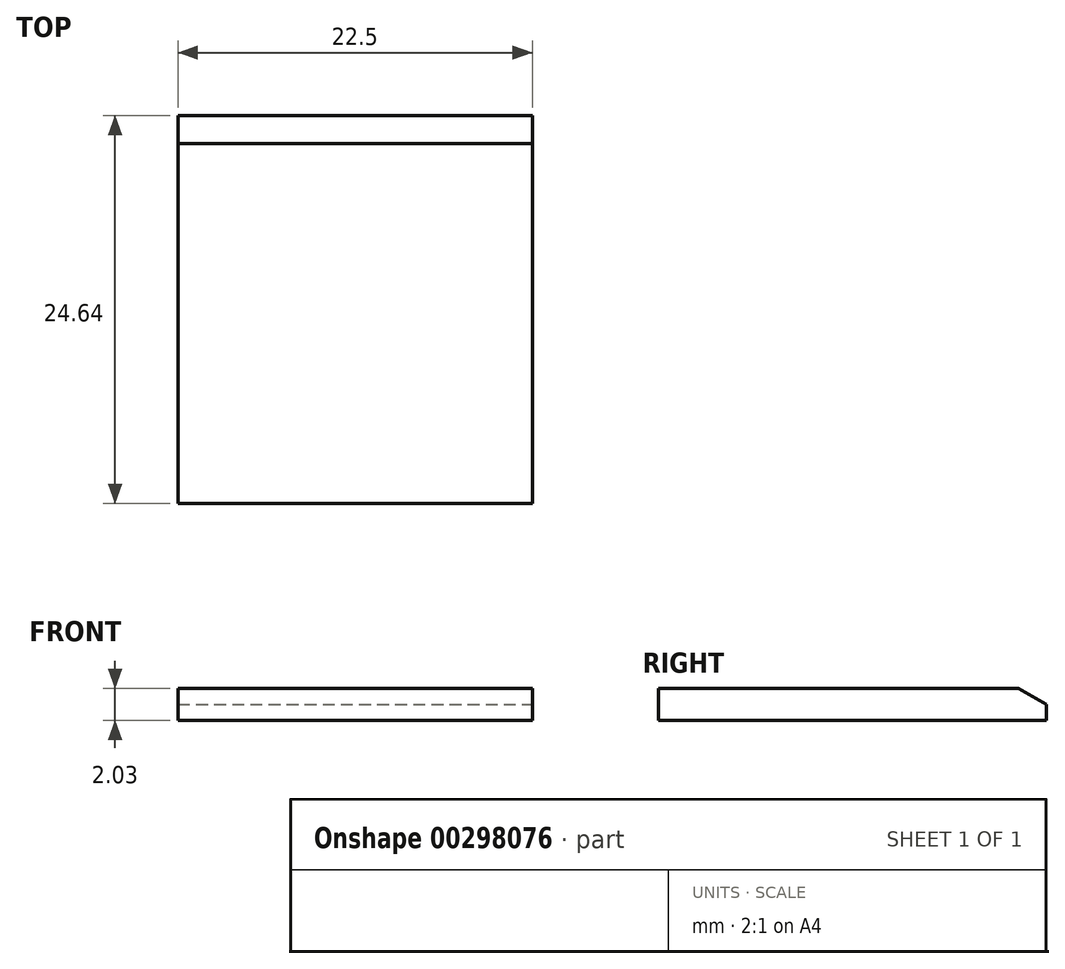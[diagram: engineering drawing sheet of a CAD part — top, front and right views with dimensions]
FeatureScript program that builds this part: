
annotation { "Feature Type Name" : "Feature", "Feature Type Description" : "" }
export const myFeature = defineFeature(function(context is Context, id is Id, definition is map)
    precondition{}
    {
        {
            var Q0;
            Q0=qCreatedBy(makeId("Front.planeOp"),FACE);
            var sketch = newSketch(context, id + "F0", { "sketchPlane" : qUnion([Q0])});
            skLineSegment(sketch, "E0.bottom", {"start": v(11.43, 1.27) * mm, "end": v(-11.43, 1.27) * mm});
            skLineSegment(sketch, "E0.top", {"start": v(11.43, -1.27) * mm, "end": v(-11.43, -1.27) * mm});
            skLineSegment(sketch, "E0.left", {"start": v(11.43, 1.27) * mm, "end": v(11.43, -1.27) * mm});
            skLineSegment(sketch, "E0.right", {"start": v(-11.43, 1.27) * mm, "end": v(-11.43, -1.27) * mm});
            skPoint(sketch, "E0.middle", {"position": v(0, 0) * mm});
            skSolve(sketch);
        }
        {
            var Q0;
            Q0=makeQuery(id+"F0.imprint","IMPRINT",FACE,{"disambiguationData":[TD([[makeQuery(id+"F0.imprint","IMPRINT",EDGE,{"derivedFrom":sQuery(id+"F0.wireOp",EDGE,"E0.bottom")}),1.0]])]});
            extrude(context, id + "F1", {"entities" : qUnion([Q0]), "depth" : 24.64 * mm});
        }
        {
            var Q0;
            Q0=makeQuery(id+"F1.opExtrude","CAP_EDGE",EDGE,{"disambiguationData":[OSD([sQuery(id+"F0.wireOp",EDGE,"E0.bottom")])],"isStart":true});
            chamfer(context, id + "F2", {"entities" : qUnion([Q0]), "chamferType" : ChamferType.OFFSET_ANGLE, "width" : 1.78 * mm, "oppositeDirection" : false, "angle" : 30 * degree, "tangentPropagation" : true});
        }
        {
            var Q0;
            Q0=makeQuery(id+"F1.opExtrude","SWEPT_FACE",FACE,{"disambiguationData":[OSD([sQuery(id+"F0.wireOp",EDGE,"E0.bottom")])]});
            var Q1;
            Q1=makeQuery(id+"F2.opChamfer","BLEND_FACE",FACE,{"disambiguationData":[OSD([sQuery(id+"F0.wireOp",EDGE,"E0.bottom")])]});
            extrude(context, id + "F3", {"entities" : qUnion([Q0, Q1]), "operationType" : NewBodyOperationType.REMOVE, "oppositeDirection" : true, "depth" : 0.5 * mm});
        }
        {
            var Q0;
            Q0=makeQuery(id+"F1.opExtrude","SWEPT_FACE",FACE,{"disambiguationData":[OSD([sQuery(id+"F0.wireOp",EDGE,"E0.right")])]});
            extrude(context, id + "F4", {"entities" : qUnion([Q0]), "operationType" : NewBodyOperationType.REMOVE, "oppositeDirection" : true, "depth" : 0.18 * mm});
        }
        {
            var Q0;
            Q0=makeQuery(id+"F1.opExtrude","SWEPT_FACE",FACE,{"disambiguationData":[OSD([sQuery(id+"F0.wireOp",EDGE,"E0.left")])]});
            extrude(context, id + "F5", {"entities" : qUnion([Q0]), "operationType" : NewBodyOperationType.REMOVE, "oppositeDirection" : true, "depth" : 0.18 * mm});
        }
    });
